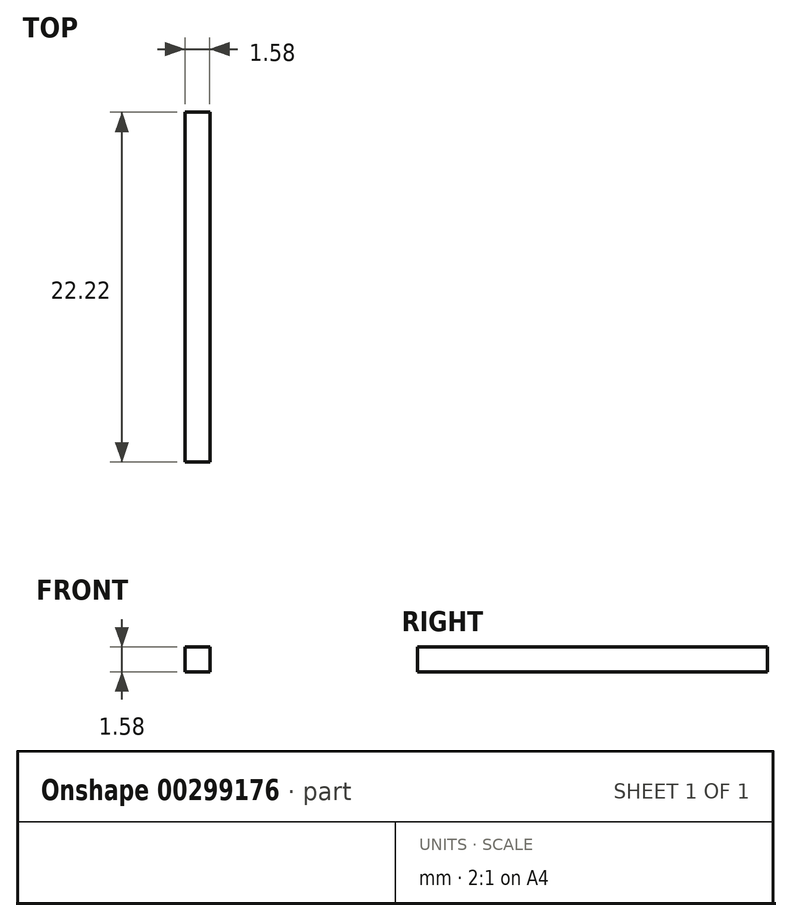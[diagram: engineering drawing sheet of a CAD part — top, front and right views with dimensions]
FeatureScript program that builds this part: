
annotation { "Feature Type Name" : "Feature", "Feature Type Description" : "" }
export const myFeature = defineFeature(function(context is Context, id is Id, definition is map)
    precondition{}
    {
        {
            var Q0;
            Q0=qCreatedBy(makeId("Front.planeOp"),FACE);
            var sketch = newSketch(context, id + "F0", { "sketchPlane" : qUnion([Q0])});
            skLineSegment(sketch, "E0.bottom", {"start": v(0.8, 0.8) * mm, "end": v(-0.8, 0.8) * mm});
            skLineSegment(sketch, "E0.top", {"start": v(0.8, -0.8) * mm, "end": v(-0.8, -0.8) * mm});
            skLineSegment(sketch, "E0.left", {"start": v(0.8, 0.8) * mm, "end": v(0.8, -0.8) * mm});
            skLineSegment(sketch, "E0.right", {"start": v(-0.8, 0.8) * mm, "end": v(-0.8, -0.8) * mm});
            skPoint(sketch, "E0.middle", {"position": v(0, 0) * mm});
            skSolve(sketch);
        }
        {
            var Q0;
            Q0 = qSketchRegion(id + "F0", true);
            extrude(context, id + "F1", {"entities" : qUnion([Q0]), "endBound" : BoundingType.SYMMETRIC, "depth" : 22.22 * mm});
        }
    });
